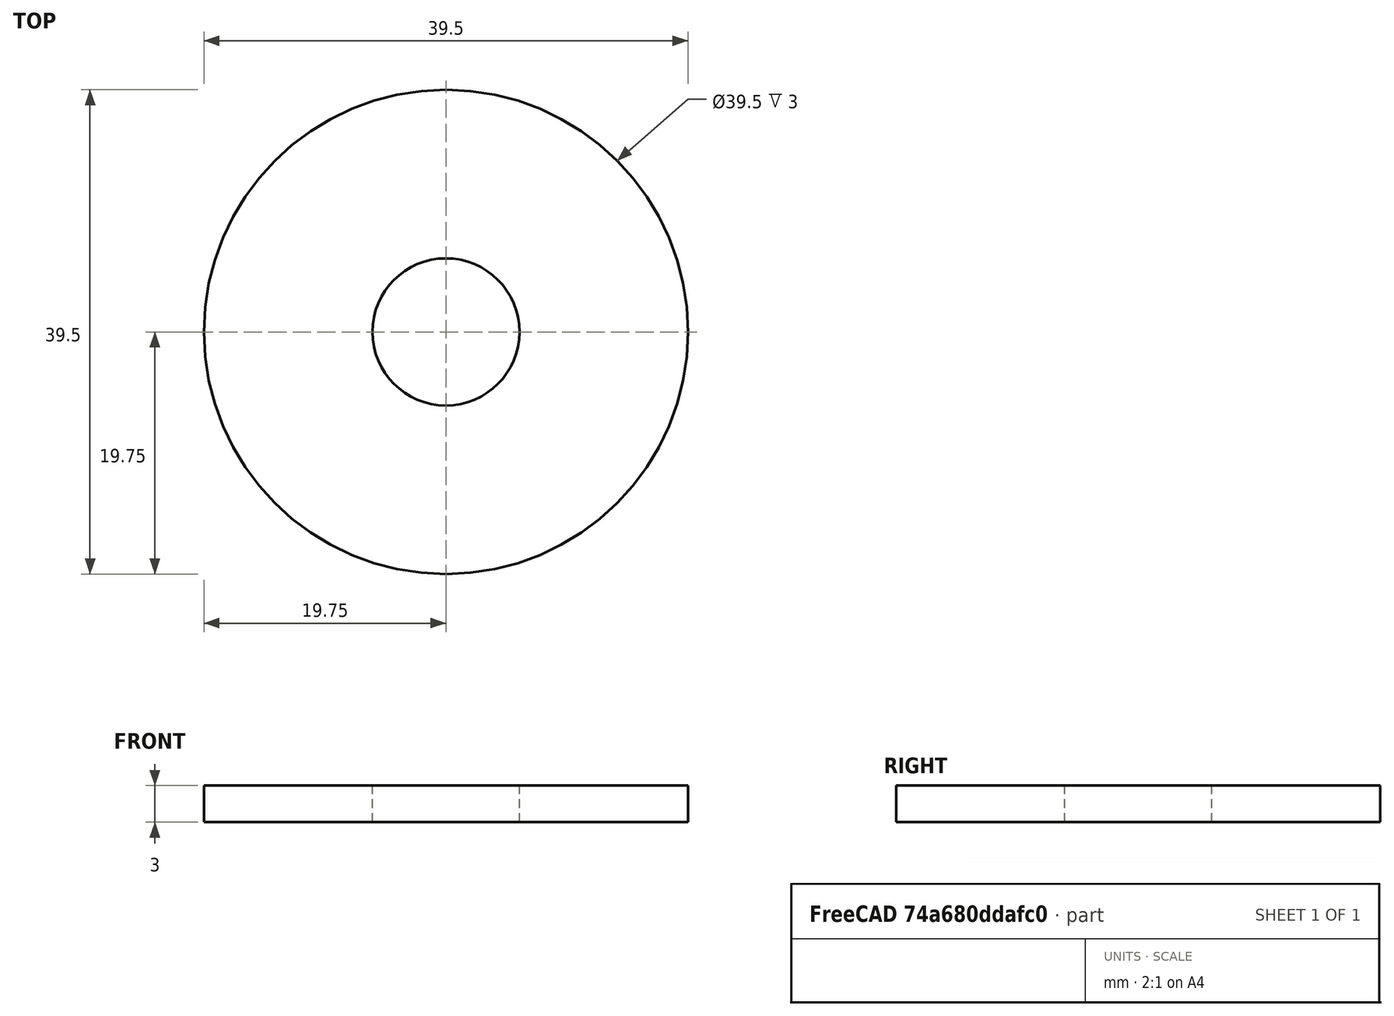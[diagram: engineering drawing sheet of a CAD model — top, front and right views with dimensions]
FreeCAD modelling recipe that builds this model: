
FCSTD DOCUMENT  (FreeCAD 0.14R3700 (Git))
Label: BIRR_pignonPCB
License: CC-BY 3.0
LicenseURL: http://creativecommons.org/licenses/by/3.0/
objects: Sketcher::SketchObject×1, Part::Revolution×1, Part::Feature×1
note: 3 computed .brp shape members not serialized (recipe doc carries the construction recipe); baked Part::Feature solids carry a one-line shape summary decoded from their .brp

FEATURE [Sketcher::SketchObject] Sketch  label="PignonPCB"
  Placement = pos=(0,0,0) rot=(1,0,0;1.5708rad)
  sketch-geometry (4):
    g0: LineSegment StartX=6 StartY=1.5 StartZ=0 EndX=19.75 EndY=1.5 EndZ=0
    g1: LineSegment StartX=19.75 StartY=1.5 StartZ=0 EndX=19.75 EndY=-1.5 EndZ=0
    g2: LineSegment StartX=19.75 StartY=-1.5 StartZ=0 EndX=6 EndY=-1.5 EndZ=0
    g3: LineSegment StartX=6 StartY=-1.5 StartZ=0 EndX=6 EndY=1.5 EndZ=0
  constraints (12):
    c: Coincident(g0,g1)
    c: Coincident(g1,g2)
    c: Coincident(g2,g3)
    c: Coincident(g3,g0)
    c: Horizontal(g0)
    c: Horizontal(g2)
    c: Vertical(g1)
    c: Vertical(g3)
    c: Symmetric(g1,g0,g-1)
    c: DistanceY(g1) = -3
    c: DistanceX(g-1,g2) = 6
    c: DistanceX(g-1,g1) = 19.75
FEATURE [Part::Revolution] Revolve
  Angle = 360
  Axis = (0,0,1)
  Base = (0,0,0)
  Solid = false
  Source = -> Sketch
FEATURE [Part::Feature] Revolve001  label="pignonPCB_copy"
  shape: bbox 39.5 x 39.5 x 3 mm, 4 faces, 0 solids (baked)
